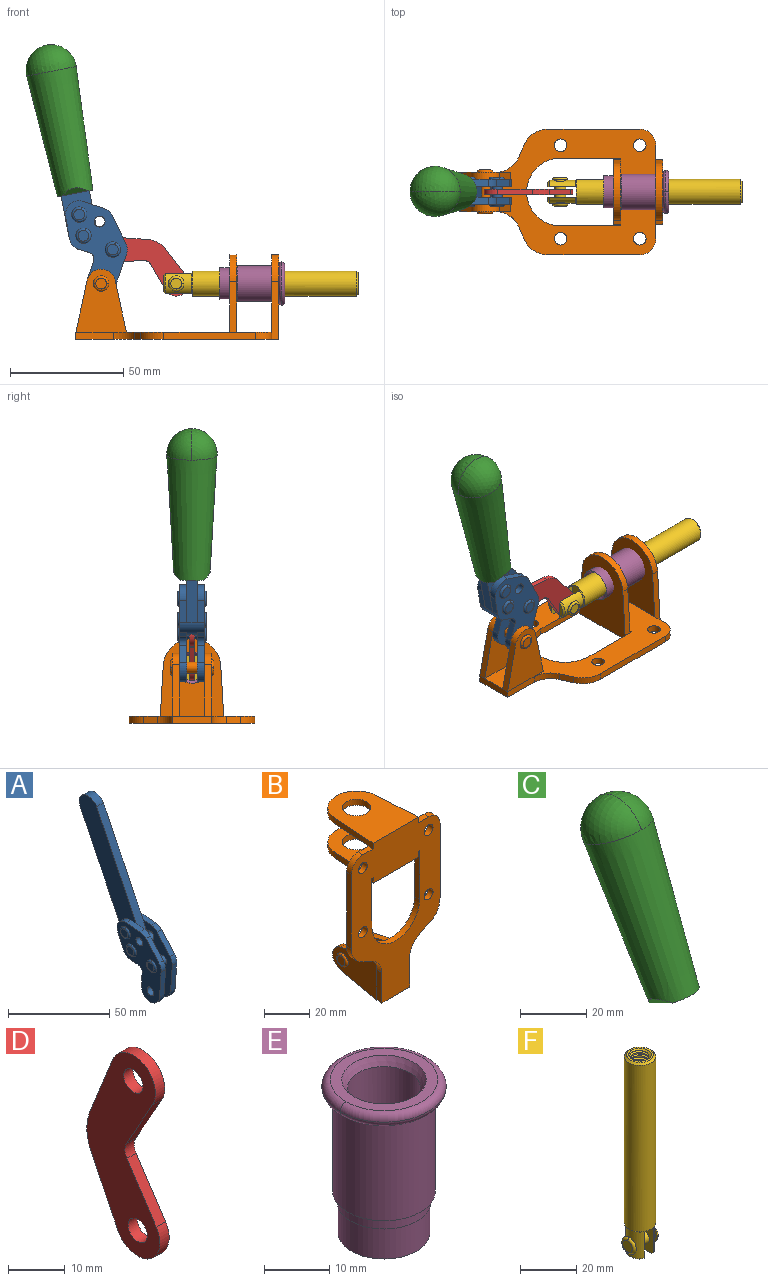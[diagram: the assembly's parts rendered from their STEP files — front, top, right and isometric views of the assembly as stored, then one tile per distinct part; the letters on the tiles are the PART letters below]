
ASSEMBLY  parts=6 mates=6
PART A: 59 faces, bbox 12.9x60.2x99.6 mm
  f0: torus R=2.39mm, axis (-1,0,0), area 14.9mm2, adj f20,f43,f51
  f1: torus R=2.39mm, axis (-1,0,0), area 14.9mm2, adj f19,f42,f51
  f2: torus R=2.39mm, axis (-1,0,0), area 14.9mm2, adj f18,f35,f51
  f3: torus R=2.39mm, axis (-1,0,0), area 14.9mm2, adj f14,f17,f23
  f4: torus R=2.39mm, axis (-1,0,0), area 14.9mm2, adj f13,f16,f23
  f5: torus R=2.39mm, axis (-1,0,0), area 14.9mm2, adj f12,f15,f23
  f6: cylinder r=2.39mm len=4.78mm, axis (1,0,0), area 46.5mm2, adj f48,f50,f51
  f7: cylinder r=2.39mm len=4.78mm, axis (1,0,0), area 46.5mm2, adj f50,f51
  f8: cylinder r=6.35mm len=12.68mm, axis (1,0,0), area 61.8mm2, adj f38,f39,f50,f51
  f9: cylinder r=2.39mm len=4.78mm, axis (-1,0,0), area 70.5mm2, adj f46,f50
  f10: cylinder r=2.39mm len=4.78mm, axis (-1,0,0), area 46.5mm2, adj f23,f45,f46
  f11: cylinder r=2.39mm len=4.78mm, axis (-1,0,0), area 46.5mm2, adj f23,f46
  f12: plane 4.78x4.78mm, normal (1,0,0), area 17.9mm2, adj f5,f15
  f13: plane 4.78x4.78mm, normal (1,0,0), area 17.9mm2, adj f4,f16
  f14: plane 4.78x4.78mm, normal (1,0,0), area 17.9mm2, adj f3,f17
  f15: torus R=2.39mm, axis (-1,0,0), area 14.9mm2, adj f5,f12,f23
  f16: torus R=2.39mm, axis (-1,0,0), area 14.9mm2, adj f4,f13,f23
  f17: torus R=2.39mm, axis (-1,0,0), area 14.9mm2, adj f3,f14,f23
  f18: plane 4.78x4.78mm, normal (-1,0,0), area 17.9mm2, adj f2,f35
  f19: plane 4.78x4.78mm, normal (-1,0,0), area 17.9mm2, adj f1,f42
  f20: plane 4.78x4.78mm, normal (-1,0,0), area 17.9mm2, adj f0,f43
  f21: plane 2.26x0.2mm, normal (1,0,0), area 0.2mm2, adj f31,f44
  f22: plane 2.26x0.2mm, normal (-1,0,0), area 0.2mm2, adj f41,f44
  f23: plane 39.37x30.77mm, normal (1,0,0), area 565.5mm2, adj f3,f4,f5,f10,f11,f15,f16,f17
  f24: cylinder r=6.1mm len=4.15mm, axis (-1,0,0), area 14.7mm2, adj f23,f25,f32,f46
  f25: plane 10.25x9.01mm, normal (0,-0.75,0.66), area 42.3mm2, adj f23,f24,f26,f46
  f26: cylinder r=6.35mm len=4.64mm, axis (-1,0,0), area 15.6mm2, adj f23,f25,f27,f46
  f27: plane 15.84x3.1mm, normal (0,-1,-0.07), area 49.2mm2, adj f23,f26,f28,f46
  f28: cylinder r=6.35mm len=12.68mm, axis (-1,0,0), area 61.8mm2, adj f23,f27,f29,f46
  f29: plane 8.11x3.1mm, normal (0,1,0.07), area 25.2mm2, adj f23,f28,f30,f46
  f30: cylinder r=3.05mm len=3.25mm, axis (-1,0,0), area 14.8mm2, adj f23,f29,f31,f46
  f31: plane 5.99x3.1mm, normal (0,0.07,-1), area 18.6mm2, adj f21,f23,f30,f44,f46
  f32: plane 9.5x3.1mm, normal (0,-0.07,1), area 29.5mm2, adj f23,f24,f33,f46,f47
  f33: cylinder r=6.1mm len=8.63mm, axis (-1,0,0), area 39.1mm2, adj f23,f32,f34,f47
  f34: plane 8.65x3.96mm, normal (0,0.91,-0.42), area 29.5mm2, adj f23,f33,f44,f47
  f35: torus R=2.39mm, axis (-1,0,0), area 14.9mm2, adj f2,f18,f51
  f36: plane 10.25x9.01mm, normal (0,-0.75,0.66), area 42.3mm2, adj f37,f49,f50,f51
  f37: cylinder r=6.35mm len=4.64mm, axis (1,0,0), area 15.6mm2, adj f36,f38,f50,f51
  f38: plane 15.84x3.1mm, normal (0,-1,-0.07), area 49.2mm2, adj f8,f37,f50,f51
  f39: plane 8.11x3.1mm, normal (0,1,0.07), area 25.2mm2, adj f8,f40,f50,f51
  f40: cylinder r=3.05mm len=3.25mm, axis (1,0,0), area 14.8mm2, adj f39,f41,f50,f51
  f41: plane 5.99x3.1mm, normal (0,0.07,-1), area 18.6mm2, adj f22,f40,f44,f50,f51
  f42: torus R=2.39mm, axis (-1,0,0), area 14.9mm2, adj f1,f19,f51
  f43: torus R=2.39mm, axis (-1,0,0), area 14.9mm2, adj f0,f20,f51
  f44: cylinder r=6.35mm len=12.12mm, axis (-1,0,0), area 128.9mm2, adj f21,f22,f23,f31,f34,f41,f46,f47
  f45: plane 2.65x1.35mm, normal (1,0,0), area 1mm2, adj f10,f55
  f46: plane 39.08x20.42mm, normal (-1,0,0), area 412.5mm2, adj f9,f10,f11,f24,f25,f26,f27,f28
  f47: plane 77.62x39.82mm, normal (1,0,0), area 850mm2, adj f32,f33,f34,f44,f53,f54,f55
  f48: plane 2.65x1.35mm, normal (-1,0,0), area 1mm2, adj f6,f55
  f49: cylinder r=6.1mm len=4.15mm, axis (1,0,0), area 14.7mm2, adj f36,f50,f51,f56
  f50: plane 39.08x20.42mm, normal (1,0,0), area 412.5mm2, adj f6,f7,f8,f9,f36,f37,f38,f39
  f51: plane 39.37x30.77mm, normal (-1,0,0), area 565.5mm2, adj f0,f1,f2,f6,f7,f8,f35,f36
  f52: plane 8.65x3.96mm, normal (0,0.91,-0.42), area 29.5mm2, adj f44,f51,f57,f58
  f53: plane 68.49x33.4mm, normal (0,0.9,-0.44), area 358.1mm2, adj f44,f47,f54,f58
  f54: cylinder r=6.35mm len=12.06mm, axis (1,0,0), area 93.7mm2, adj f47,f53,f55,f58
  f55: plane 68.49x33.4mm, normal (0,-0.9,0.44), area 358.1mm2, adj f44,f45,f46,f47,f48,f50,f54,f58
  f56: plane 9.5x3.1mm, normal (0,-0.07,1), area 29.5mm2, adj f49,f50,f51,f57,f58
  f57: cylinder r=6.1mm len=8.63mm, axis (1,0,0), area 39.1mm2, adj f51,f52,f56,f58
  f58: plane 77.62x39.82mm, normal (-1,0,0), area 850mm2, adj f44,f52,f53,f54,f55,f56,f57
PART B: 55 faces, bbox 55.7x37.4x89.8 mm
  f0: torus R=2.41mm, axis (-1,0,0), area 15mm2, adj f11,f15,f25
  f1: torus R=2.41mm, axis (-1,0,0), area 15mm2, adj f10,f12,f22
  f2: cylinder r=2.78mm len=5.56mm, axis (0,-1,0), area 54.2mm2, adj f30,f54
  f3: cylinder r=14.99mm len=29.97mm, axis (0,-1,0), area 145.9mm2, adj f30,f49,f53,f54
  f4: cylinder r=2.78mm len=5.56mm, axis (0,-1,0), area 54.2mm2, adj f30,f54
  f5: cylinder r=2.78mm len=5.56mm, axis (0,-1,0), area 54.2mm2, adj f30,f54
  f6: cylinder r=2.78mm len=5.56mm, axis (0,-1,0), area 54.2mm2, adj f30,f54
  f7: cylinder r=6.35mm len=12.7mm, axis (0,0,1), area 123.6mm2, adj f27,f51
  f8: cylinder r=6.35mm len=12.7mm, axis (0,0,-1), area 124.7mm2, adj f21,f35
  f9: cylinder r=2.41mm len=11.18mm, axis (-1,0,0), area 169.4mm2, adj f16,f19
  f10: plane 4.83x4.83mm, normal (1,0,0), area 18.3mm2, adj f1,f12
  f11: plane 4.83x4.83mm, normal (-1,0,0), area 18.3mm2, adj f0,f15
  f12: torus R=2.41mm, axis (-1,0,0), area 15mm2, adj f1,f10,f22
  f13: cylinder r=6.35mm len=12.41mm, axis (1,0,0), area 53.4mm2, adj f18,f19,f22,f23
  f14: cylinder r=6.35mm len=12.41mm, axis (-1,0,0), area 53.4mm2, adj f16,f17,f24,f25
  f15: torus R=2.41mm, axis (-1,0,0), area 15mm2, adj f0,f11,f25
  f16: plane 27.86x22.35mm, normal (1,0,0), area 425.4mm2, adj f9,f14,f17,f24,f30
  f17: plane 22.86x4.97mm, normal (0,0.21,0.98), area 72.5mm2, adj f14,f16,f25,f30
  f18: plane 22.86x4.97mm, normal (0,0.21,0.98), area 72.5mm2, adj f13,f19,f22,f30
  f19: plane 27.86x22.35mm, normal (-1,0,0), area 425.4mm2, adj f9,f13,f18,f23,f30
  f20: cylinder r=12.7mm len=25.35mm, axis (0,0,-1), area 119.8mm2, adj f21,f34,f35,f36
  f21: plane 34.21x28.07mm, normal (0,0,-1), area 702.4mm2, adj f8,f20,f30,f34,f36
  f22: plane 27.96x22.45mm, normal (1,0,0), area 407.2mm2, adj f1,f12,f13,f18,f23,f30,f42,f43
  f23: plane 22.86x4.97mm, normal (0,0.21,-0.98), area 72.5mm2, adj f13,f19,f22,f44
  f24: plane 22.86x4.97mm, normal (0,0.21,-0.98), area 72.5mm2, adj f14,f16,f25,f44
  f25: plane 27.86x22.35mm, normal (-1,0,0), area 407.1mm2, adj f0,f14,f15,f17,f24,f30,f45,f46
  f26: plane 3.1x0.95mm, normal (0,0,-1), area 2.7mm2, adj f30,f49,f50,f54
  f27: plane 34.21x28.07mm, normal (0,0,1), area 702.4mm2, adj f7,f28,f30,f50,f52
  f28: cylinder r=12.7mm len=25.35mm, axis (0,0,1), area 118.8mm2, adj f27,f50,f51,f52
  f29: plane 3.1x0.95mm, normal (0,0,-1), area 2.7mm2, adj f30,f52,f53,f54
  f30: plane 86.54x55.63mm, normal (0,1,0), area 2362.9mm2, adj f2,f3,f4,f5,f6,f16,f17,f18
  f31: plane 40.56x3.1mm, normal (-1,0,0), area 125.7mm2, adj f30,f32,f48,f54
  f32: cylinder r=7.11mm len=7.11mm, axis (0,-1,0), area 34.6mm2, adj f30,f31,f33,f54
  f33: plane 6.67x3.1mm, normal (0,0,1), area 20.4mm2, adj f30,f32,f34,f54
  f34: plane 25.39x3.13mm, normal (-1,0.06,0), area 79.5mm2, adj f20,f21,f33,f35,f54
  f35: plane 37.31x28.45mm, normal (0,0,1), area 789.9mm2, adj f8,f20,f34,f36,f54
  f36: plane 25.39x3.13mm, normal (1,0.06,0), area 79.5mm2, adj f20,f21,f35,f37,f54
  f37: plane 6.67x3.1mm, normal (0,0,1), area 20.4mm2, adj f30,f36,f38,f54
  f38: cylinder r=7.11mm len=7.11mm, axis (0,-1,0), area 34.6mm2, adj f30,f37,f39,f54
  f39: plane 40.56x3.1mm, normal (1,0,0), area 125.7mm2, adj f30,f38,f40,f54
  f40: cylinder r=11.18mm len=10.16mm, axis (0,-1,0), area 39.5mm2, adj f30,f39,f41,f54
  f41: plane 6.09x3.1mm, normal (0.42,0,-0.91), area 20.8mm2, adj f30,f40,f42,f54
  f42: cylinder r=11.18mm len=9.41mm, axis (0,-1,0), area 37.2mm2, adj f22,f30,f41,f43,f54
  f43: plane 16.5x3.1mm, normal (1,0,0), area 51.1mm2, adj f22,f42,f44,f54
  f44: plane 17.37x3.1mm, normal (0,0,-1), area 53.8mm2, adj f23,f24,f30,f43,f45,f54
  f45: plane 16.5x3.1mm, normal (-1,0,0), area 51.1mm2, adj f25,f44,f46,f54
  f46: cylinder r=11.18mm len=9.41mm, axis (0,-1,0), area 37.2mm2, adj f25,f30,f45,f47,f54
  f47: plane 6.09x3.1mm, normal (-0.42,0,-0.91), area 20.8mm2, adj f30,f46,f48,f54
  f48: cylinder r=11.18mm len=10.16mm, axis (0,-1,0), area 39.5mm2, adj f30,f31,f47,f54
  f49: plane 26.54x3.1mm, normal (-1,0,0), area 82.3mm2, adj f3,f26,f30,f54
  f50: plane 25.39x3.1mm, normal (1,0.06,0), area 78.8mm2, adj f26,f27,f28,f51,f54
  f51: plane 37.31x28.45mm, normal (0,0,-1), area 789.9mm2, adj f7,f28,f50,f52,f54
  f52: plane 25.39x3.1mm, normal (-1,0.06,0), area 78.8mm2, adj f27,f28,f29,f51,f54
  f53: plane 26.54x3.1mm, normal (1,0,0), area 82.3mm2, adj f3,f29,f30,f54
  f54: plane 89.66x55.63mm, normal (0,-1,0), area 2678.5mm2, adj f2,f3,f4,f5,f6,f26,f29,f31
PART C: 11 faces, bbox 22.3x42.6x64.5 mm
  f0: sphere r=11.13mm, area 411.4mm2, adj f1,f8
  f1: cone r=11.11mm half-angle=3.3deg, axis (0,0.44,0.9), area 3251.8mm2, adj f0,f7,f8,f9,f10
  f2: cylinder r=6.16mm len=11.7mm, axis (1,0,0), area 89.5mm2, adj f3,f4,f5,f6
  f3: plane 60.23x36.75mm, normal (-1,0,0), area 763.6mm2, adj f2,f4,f6,f10
  f4: plane 51.37x25.05mm, normal (0,0.9,-0.44), area 264.2mm2, adj f2,f3,f5,f10
  f5: plane 60.23x36.75mm, normal (1,0,0), area 763.6mm2, adj f2,f4,f6,f10
  f6: plane 51.37x25.05mm, normal (0,-0.9,0.44), area 264.2mm2, adj f2,f3,f5,f10
  f7: plane 9.95x5.95mm, normal (0.71,-0.31,-0.64), area 25.8mm2, adj f1,f10
  f8: sphere r=11.13mm, area 411.4mm2, adj f0,f1
  f9: plane 9.95x5.95mm, normal (-0.71,-0.31,-0.64), area 25.8mm2, adj f1,f10
  f10: plane 14.27x11.38mm, normal (0,-0.44,-0.9), area 106.7mm2, adj f1,f3,f4,f5,f6,f7,f9
PART D: 12 faces, bbox 2.3x18.2x42.8 mm
  f0: cylinder r=2.4mm len=4.8mm, axis (1,0,0), area 34.9mm2, adj f4,f11
  f1: cylinder r=10.41mm len=8.47mm, axis (1,0,0), area 20.2mm2, adj f4,f9,f10,f11
  f2: cylinder r=3.05mm len=3.16mm, axis (1,0,0), area 7.7mm2, adj f4,f6,f7,f11
  f3: cylinder r=2.4mm len=4.8mm, axis (1,0,0), area 34.9mm2, adj f4,f11
  f4: plane 42.81x18.23mm, normal (-1,0,0), area 414.1mm2, adj f0,f1,f2,f3,f5,f6,f7,f8
  f5: cylinder r=5.54mm len=10.67mm, axis (1,0,0), area 41.8mm2, adj f4,f6,f10,f11
  f6: plane 11.66x6.53mm, normal (0,-0.87,-0.49), area 30.9mm2, adj f2,f4,f5,f11
  f7: plane 11.17x7.33mm, normal (0,-0.84,0.55), area 30.9mm2, adj f2,f4,f8,f11
  f8: cylinder r=5.54mm len=10.51mm, axis (1,0,0), area 41.8mm2, adj f4,f7,f9,f11
  f9: plane 13.67x6.67mm, normal (0,0.9,-0.44), area 35.1mm2, adj f1,f4,f8,f11
  f10: plane 14.1x5.7mm, normal (0,0.93,0.37), area 35.1mm2, adj f1,f4,f5,f11
  f11: plane 42.81x18.23mm, normal (1,0,0), area 414.1mm2, adj f0,f1,f2,f3,f5,f6,f7,f8
PART E: 15 faces, bbox 20.6x20.6x28.7 mm
  f0: torus R=8.26mm, axis (0,0,1), area 56.8mm2, adj f1,f10,f12
  f1: torus R=8.26mm, axis (0,0,1), area 56.8mm2, adj f0,f6,f13
  f2: cylinder r=5.59mm len=25.91mm, axis (0,0,1), area 909.6mm2, adj f3,f4
  f3: cone r=6.86mm half-angle=45deg, axis (0,0,-1), area 70.2mm2, adj f2,f14
  f4: cone r=6.47mm half-angle=30deg, axis (0,0,1), area 66.7mm2, adj f2,f13
  f5: cylinder r=7.04mm len=14.07mm, axis (0,0,1), area 252.6mm2, adj f11,f14
  f6: torus R=8.26mm, axis (0,0,1), area 56.8mm2, adj f1,f12,f13
  f7: cylinder r=7.16mm len=14.33mm, axis (0,0,1), area 91.5mm2, adj f9,f11
  f8: cylinder r=7.86mm len=18.42mm, axis (0,0,1), area 909.6mm2, adj f9,f10
  f9: plane 15.72x15.72mm, normal (0,0,-1), area 33mm2, adj f7,f8
  f10: plane 16.51x16.51mm, normal (0,0,-1), area 19.9mm2, adj f0,f8,f12
  f11: plane 14.33x14.33mm, normal (0,0,-1), area 5.7mm2, adj f5,f7
  f12: torus R=8.26mm, axis (0,0,1), area 56.8mm2, adj f0,f6,f10
  f13: plane 16.51x16.51mm, normal (0,0,1), area 82.7mm2, adj f1,f4,f6
  f14: plane 14.07x14.07mm, normal (0,0,-1), area 7.8mm2, adj f3,f5
PART F: 48 faces, bbox 12.6x11.1x86.1 mm
  f0: torus R=2.41mm, axis (-1,0,0), area 15mm2, adj f30,f32,f34
  f1: torus R=2.41mm, axis (-1,0,0), area 15mm2, adj f29,f31,f33
  f2: cylinder r=5.54mm len=72.39mm, axis (0,0,1), area 2518.5mm2, adj f3,f4,f42,f43
  f3: cone r=5.54mm half-angle=45deg, axis (0,0,1), area 7.6mm2, adj f2,f5,f41
  f4: cone r=5.54mm half-angle=45deg, axis (0,0,-1), area 34.9mm2, adj f2,f39
  f5: cylinder r=5.08mm len=11.48mm, axis (0,0,1), area 108.3mm2, adj f3,f7,f8,f41
  f6: cylinder r=2.41mm len=4.83mm, axis (-1,0,0), area 71.2mm2, adj f40,f41
  f7: cylinder r=2.41mm len=4.83mm, axis (-1,0,0), area 7.6mm2, adj f5,f34
  f8: cone r=5.08mm half-angle=45deg, axis (0,0,1), area 10.6mm2, adj f5,f37,f41
  f9: cone r=3.98mm half-angle=45deg, axis (0,0,1), area 17.6mm2, adj f27,f39,f45,f46,f47
  f10: cylinder r=2.41mm len=4.83mm, axis (-1,0,0), area 7.6mm2, adj f33,f38
  f11: cylinder r=3.2mm len=6.4mm, axis (0,0,1), area 78.4mm2, adj f12,f28,f44,f45,f47
  f12: cylinder r=3.2mm len=6.4mm, axis (0,0,1), area 10.5mm2, adj f11,f13,f45,f47
  f13: cylinder r=3.2mm len=6.4mm, axis (0,0,1), area 10.5mm2, adj f12,f14,f45,f47
  f14: cylinder r=3.2mm len=6.4mm, axis (0,0,1), area 10.5mm2, adj f13,f15,f45,f47
  f15: cylinder r=3.2mm len=6.4mm, axis (0,0,1), area 10.5mm2, adj f14,f16,f45,f47
  f16: cylinder r=3.2mm len=6.4mm, axis (0,0,1), area 10.5mm2, adj f15,f17,f45,f47
  f17: cylinder r=3.2mm len=6.4mm, axis (0,0,1), area 10.5mm2, adj f16,f18,f45,f47
  f18: cylinder r=3.2mm len=6.4mm, axis (0,0,1), area 10.5mm2, adj f17,f19,f45,f47
  f19: cylinder r=3.2mm len=6.4mm, axis (0,0,1), area 10.5mm2, adj f18,f20,f45,f47
  f20: cylinder r=3.2mm len=6.4mm, axis (0,0,1), area 10.5mm2, adj f19,f21,f45,f47
  f21: cylinder r=3.2mm len=6.4mm, axis (0,0,1), area 10.5mm2, adj f20,f22,f45,f47
  f22: cylinder r=3.2mm len=6.4mm, axis (0,0,1), area 10.5mm2, adj f21,f23,f45,f47
  f23: cylinder r=3.2mm len=6.4mm, axis (0,0,1), area 10.5mm2, adj f22,f24,f45,f47
  f24: cylinder r=3.2mm len=6.4mm, axis (0,0,1), area 10.5mm2, adj f23,f25,f45,f47
  f25: cylinder r=3.2mm len=6.4mm, axis (0,0,1), area 10.5mm2, adj f24,f26,f45,f47
  f26: cylinder r=3.2mm len=6.4mm, axis (0,0,1), area 10.5mm2, adj f25,f27,f45,f47
  f27: cylinder r=3.2mm len=6.4mm, axis (0,0,1), area 7.4mm2, adj f9,f26,f45,f47
  f28: cone r=3.2mm half-angle=60deg, axis (0,0,1), area 37.2mm2, adj f11
  f29: plane 4.83x4.83mm, normal (-1,0,0), area 18.3mm2, adj f1,f31
  f30: plane 4.83x4.83mm, normal (1,0,0), area 18.3mm2, adj f0,f32
  f31: torus R=2.41mm, axis (-1,0,0), area 15mm2, adj f1,f29,f33
  f32: torus R=2.41mm, axis (-1,0,0), area 15mm2, adj f0,f30,f34
  f33: plane 6.83x6.83mm, normal (1,0,0), area 18.3mm2, adj f1,f10,f31
  f34: plane 6.83x6.83mm, normal (-1,0,0), area 18.3mm2, adj f0,f7,f32
  f35: cone r=5.08mm half-angle=45deg, axis (0,0,1), area 10.6mm2, adj f36,f38,f40
  f36: plane 7.25x1.97mm, normal (0,0,-1), area 10mm2, adj f35,f40
  f37: plane 7.25x1.97mm, normal (0,0,-1), area 10mm2, adj f8,f41
  f38: cylinder r=5.08mm len=11.48mm, axis (0,0,1), area 108.3mm2, adj f10,f35,f40,f42
  f39: plane 9.55x9.55mm, normal (0,0,1), area 22mm2, adj f4,f9
  f40: plane 12.76x10.09mm, normal (1,0,0), area 95.7mm2, adj f6,f35,f36,f38,f42,f43
  f41: plane 12.76x10.09mm, normal (-1,0,0), area 95.7mm2, adj f3,f5,f6,f8,f37,f43
  f42: cone r=5.54mm half-angle=45deg, axis (0,0,1), area 7.6mm2, adj f2,f38,f40
  f43: plane 11.07x4.7mm, normal (0,0,-1), area 50.4mm2, adj f2,f40,f41
  f44: plane 0.89x0.62mm, normal (-1,0,0), area 0.3mm2, adj f11,f45,f46,f47
  f45: bspline ~24.8x7.63mm, area 266.6mm2, adj f9,f11,f12,f13,f14,f15,f16,f17
  f46: bspline ~24.87x7.63mm, area 73.6mm2, adj f9,f44,f45,f47
  f47: bspline ~24.98x7.63mm, area 272.5mm2, adj f9,f11,f12,f13,f14,f15,f16,f17
PLACE A rot(axis=(0.13,0.13,0.98),91deg) t=(-1.57,0,30.59)mm
PLACE B rot(axis=(0.58,0.58,0.58),120deg) t=(-1.56,0,-18.66)mm fixed
PLACE C rot(axis=(0.13,0.13,0.98),91deg) t=(-1.57,0.04,30.59)mm
PLACE D rot(axis=(0.47,-0.47,-0.75),106.2deg) t=(-25.47,0,-7.95)mm
PLACE E rot(axis=(0.71,0,0.71),180deg) t=(-1.56,24.61,5.96)mm
PLACE F rot(axis=(-0.58,0.58,-0.58),120deg) t=(-15.98,0,30.57)mm
MATE fastened E.f2 <-> B.f7  axis (-1,0,0) through (44.83,0,5.96)mm
MATE revolute D.f3 <-> F.f6  axis (0,-1,0) through (-0.51,0,5.96)mm
MATE revolute D.f5 <-> A.f4  axis (0,-1,0) through (-28.49,0,20.97)mm
MATE revolute A.f7 <-> B.f0  axis (0,-1,0) through (-33.65,0,5.96)mm
MATE fastened A.f54 <-> C.f2  axis (0,1,0) through (-56.02,2.35,101.88)mm
MATE slider F.f2 <-> E.f2  axis (1,0,0) through (42.8,0,5.96)mm
